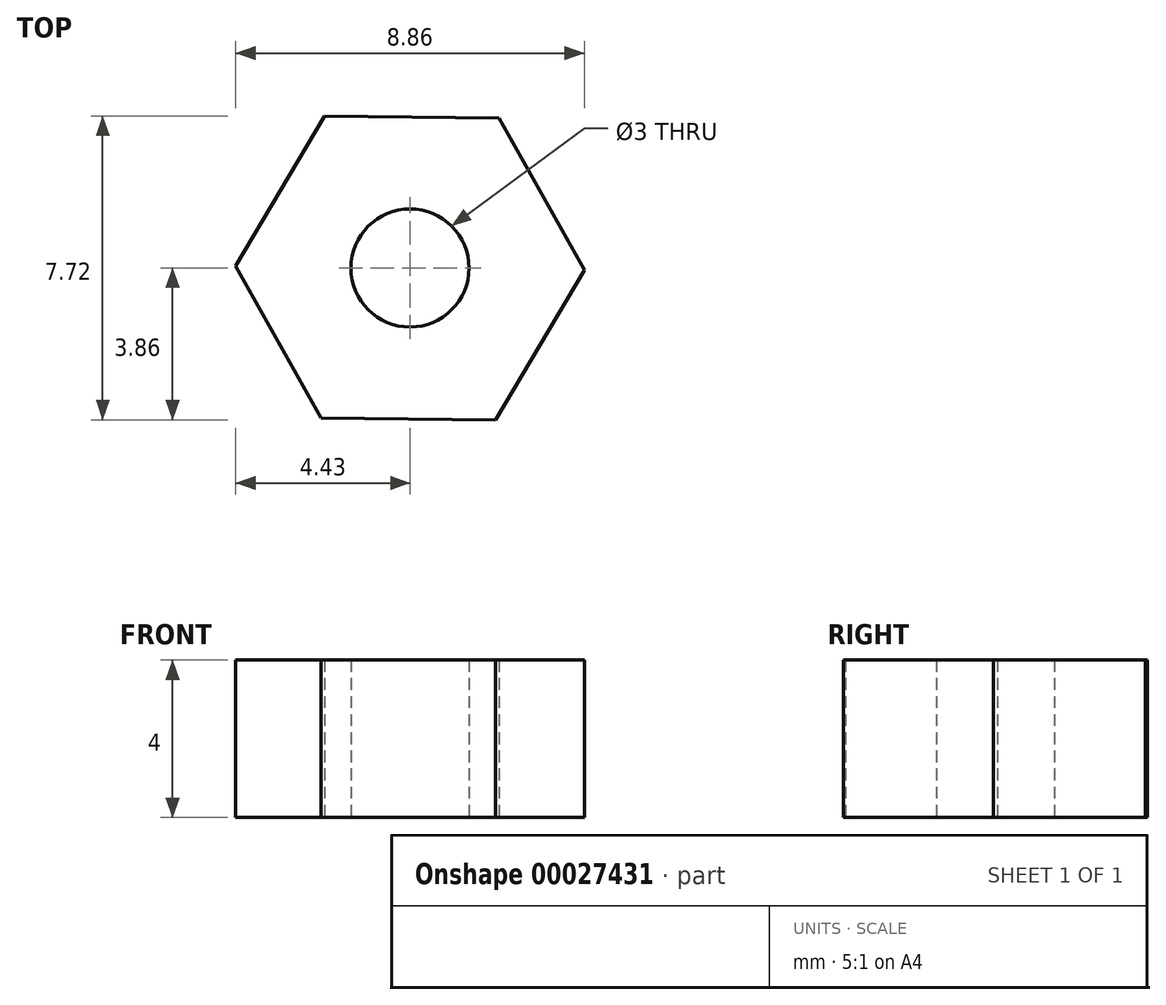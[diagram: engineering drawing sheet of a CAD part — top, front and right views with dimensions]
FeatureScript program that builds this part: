
annotation { "Feature Type Name" : "Feature", "Feature Type Description" : "" }
export const myFeature = defineFeature(function(context is Context, id is Id, definition is map)
    precondition{}
    {
        {
            var Q0;
            Q0=qCreatedBy(makeId("Top.planeOp"),FACE);
            var sketch = newSketch(context, id + "F0", { "sketchPlane" : qUnion([Q0])});
            skCircle(sketch, "E0.cCircle", {"center": v(0, 0) * mm, "radius": 3.84 * mm, "construction": true});
            skLineSegment(sketch, "E0.0", {"start": v(4.43, -0.05) * mm, "end": v(2.17, -3.86) * mm});
            skLineSegment(sketch, "E0.1", {"start": v(2.17, -3.86) * mm, "end": v(-2.26, -3.8) * mm});
            skLineSegment(sketch, "E0.2", {"start": v(-2.26, -3.8) * mm, "end": v(-4.43, 0.05) * mm});
            skLineSegment(sketch, "E0.3", {"start": v(-4.43, 0.05) * mm, "end": v(-2.17, 3.86) * mm});
            skLineSegment(sketch, "E0.4", {"start": v(-2.17, 3.86) * mm, "end": v(2.26, 3.8) * mm});
            skLineSegment(sketch, "E0.5", {"start": v(2.26, 3.8) * mm, "end": v(4.43, -0.05) * mm});
            skPoint(sketch, "E0.0.midPoint", {"position": v(3.3, -1.96) * mm});
            skCircle(sketch, "E1", {"center": v(0, 0) * mm, "radius": 1.5 * mm});
            skSolve(sketch);
        }
        {
            var Q0;
            Q0=makeQuery(id+"F0.imprint","IMPRINT",FACE,{"disambiguationData":[TD([[makeQuery(id+"F0.imprint","IMPRINT",EDGE,{"derivedFrom":sQuery(id+"F0.wireOp",EDGE,"E0.0")}),-1.0]])]});
            extrude(context, id + "F1", {"entities" : qUnion([Q0]), "depth" : 4 * mm});
        }
    });
